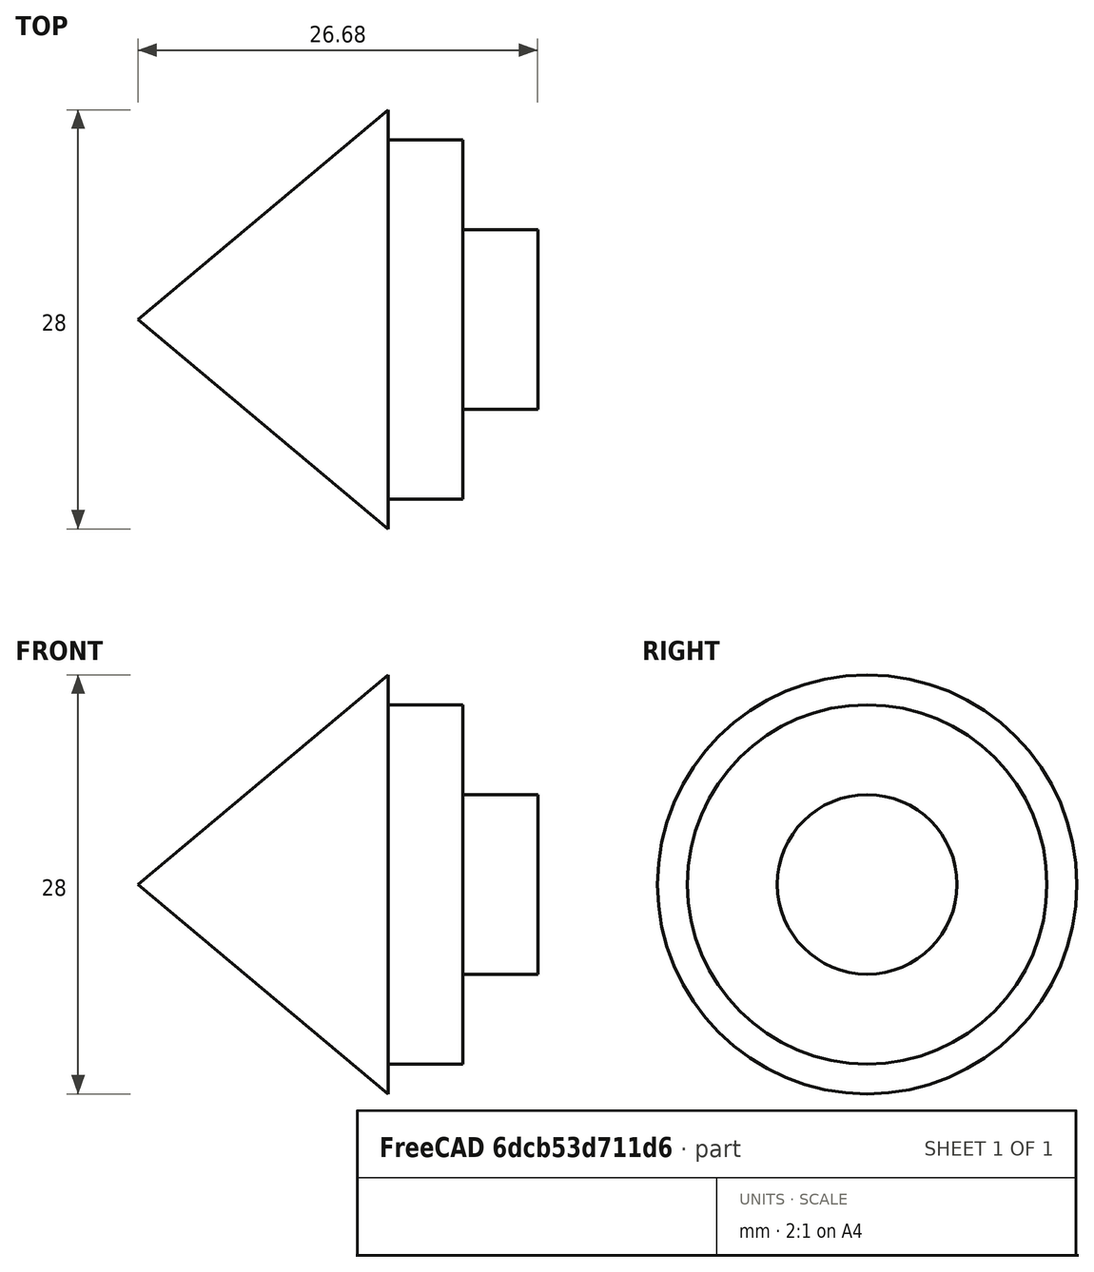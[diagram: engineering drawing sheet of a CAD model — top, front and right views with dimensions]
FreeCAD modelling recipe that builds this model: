
FCSTD DOCUMENT  (FreeCAD 0.19R)
Label: head
License: All rights reserved
LicenseURL: http://en.wikipedia.org/wiki/All_rights_reserved
objects: Sketcher::SketchObject×1, PartDesign::Revolution×1, PartDesign::Body×1
note: 4 computed .brp shape members not serialized (recipe doc carries the construction recipe); baked Part::Feature solids carry a one-line shape summary decoded from their .brp

FEATURE [Sketcher::SketchObject] Sketch
  MapMode = 5
  Support = -> [XY_Plane]
  sketch-geometry (7):
    g0: LineSegment StartX=0 StartY=0 StartZ=0 EndX=16.6846 EndY=14 EndZ=0
    g1: LineSegment StartX=16.6846 StartY=14 StartZ=0 EndX=16.6846 EndY=12 EndZ=0
    g2: LineSegment StartX=16.6846 StartY=12 StartZ=0 EndX=21.6846 EndY=12 EndZ=0
    g3: LineSegment StartX=21.6846 StartY=12 StartZ=0 EndX=21.6846 EndY=6 EndZ=0
    g4: LineSegment StartX=21.6846 StartY=6 StartZ=0 EndX=26.6846 EndY=6 EndZ=0
    g5: LineSegment StartX=26.6846 StartY=6 StartZ=0 EndX=26.6846 EndY=0 EndZ=0
    g6: LineSegment StartX=26.6846 StartY=0 StartZ=0 EndX=0 EndY=0 EndZ=0
  constraints (20):
    c: Coincident(g0,g-1)
    c: Coincident(g1,g0)
    c: Vertical(g1)
    c: Coincident(g2,g1)
    c: Horizontal(g2)
    c: Coincident(g3,g2)
    c: Vertical(g3)
    c: Coincident(g4,g3)
    c: Horizontal(g4)
    c: Coincident(g5,g4)
    c: PointOnObject(g5,g-1)
    c: Vertical(g5)
    c: Coincident(g6,g5)
    c: Coincident(g6,g0)
    c: Distance(g0,g6) = 14
    c: Distance(g5) = 6
    c: Angle(g6,g0) = 0.698132
    c: Distance(g2) = 5
    c: Distance(g4) = 5
    c: Distance(g5,g2) = 12
FEATURE [PartDesign::Revolution] Revolution
  AllowMultiFace = false
  Angle = 360
  Axis = (1,0,0)
  Base = (0,0,0)
  Profile = -> Sketch
  ReferenceAxis = -> Sketch [H_Axis]
FEATURE [PartDesign::Body] Body
  Group = -> [Sketch,Revolution]
  Origin = -> Origin
  Tip = -> Revolution
